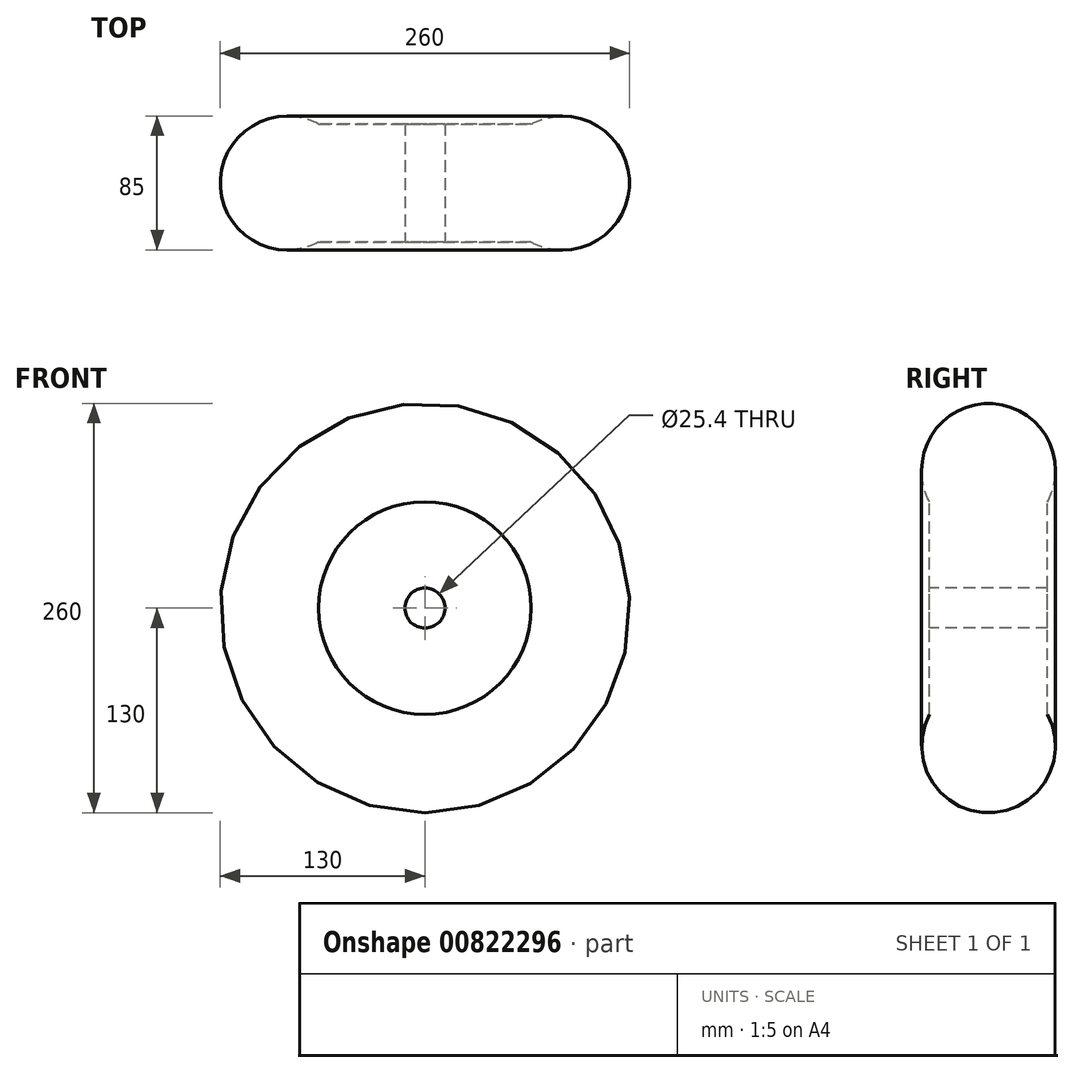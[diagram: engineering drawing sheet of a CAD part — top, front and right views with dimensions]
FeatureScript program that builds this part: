
annotation { "Feature Type Name" : "Feature", "Feature Type Description" : "" }
export const myFeature = defineFeature(function(context is Context, id is Id, definition is map)
    precondition{}
    {
        {
            var Q0;
            Q0=qCreatedBy(makeId("Right.planeOp"),FACE);
            var sketch = newSketch(context, id + "F0", { "sketchPlane" : qUnion([Q0])});
            skLineSegment(sketch, "E0", {"start": v(0, 0) * mm, "end": v(0, 130) * mm});
            skLineSegment(sketch, "E1", {"start": v(0, 0) * mm, "end": v(37.5, 0) * mm});
            skLineSegment(sketch, "E2", {"start": v(0, 130) * mm, "end": v(42.5, 130) * mm});
            skLineSegment(sketch, "E3", {"start": v(37.5, 0) * mm, "end": v(37.5, 12.7) * mm});
            skLineSegment(sketch, "E4", {"start": v(37.5, 12.7) * mm, "end": v(0, 12.7) * mm});
            skLineSegment(sketch, "E5", {"start": v(42.5, 130) * mm, "end": v(42.5, 87.5) * mm});
            skCircle(sketch, "E6", {"center": v(0, 87.5) * mm, "radius": 42.5 * mm});
            skLineSegment(sketch, "E7", {"start": v(37.5, 12.7) * mm, "end": v(37.5, 67.5) * mm});
            skLineSegment(sketch, "E8.MirrorCS", {"start": v(0, 0) * mm, "end": v(-37.5, 0) * mm});
            skLineSegment(sketch, "E9.MirrorCS", {"start": v(-37.5, 12.7) * mm, "end": v(-37.5, 67.5) * mm});
            skLineSegment(sketch, "E10.MirrorCS", {"start": v(-37.5, 0) * mm, "end": v(-37.5, 12.7) * mm});
            skLineSegment(sketch, "E11.MirrorCS", {"start": v(-37.5, 12.7) * mm, "end": v(0, 12.7) * mm});
            skSolve(sketch);
        }
        {
            var Q0;
            {var subQ4=sQuery(id+"F0.wireOp",EDGE,"E9.MirrorCS");Q0=makeQuery(id+"F0.imprint","IMPRINT",FACE,{"disambiguationData":[TD([[makeQuery(id+"F0.imprint","IMPRINT",EDGE,{"derivedFrom":subQ4}),-1.0]])]});}
            var Q1;
            {var subQ3=sQuery(id+"F0.wireOp",EDGE,"E4");Q1=makeQuery(id+"F0.imprint","IMPRINT",FACE,{"disambiguationData":[TD([[makeQuery(id+"F0.imprint","IMPRINT",EDGE,{"derivedFrom":subQ3}),-1.0]])]});}
            var Q2;
            {var subQ0=sQuery(id+"F0.wireOp",EDGE,"E6");var subQ1=sQuery(id+"F0.wireOp",EDGE,"E0");var subQ2=makeQuery(id+"F0.imprint","INTERSECT",VERTEX,{"derivedFrom":[subQ1,subQ0]});Q2=makeQuery(id+"F0.imprint","IMPRINT",FACE,{"disambiguationData":[TD([[makeQuery(id+"F0.imprint","IMPRINT",EDGE,{"disambiguationData":[TD([[subQ2,1.0]])],"derivedFrom":subQ0}),1.0]])]});}
            var Q3;
            {var subQ0=sQuery(id+"F0.wireOp",EDGE,"E6");var subQ1=sQuery(id+"F0.wireOp",EDGE,"E0");var subQ2=makeQuery(id+"F0.imprint","INTERSECT",VERTEX,{"derivedFrom":[subQ1,subQ0]});Q3=makeQuery(id+"F0.imprint","IMPRINT",FACE,{"disambiguationData":[TD([[makeQuery(id+"F0.imprint","IMPRINT",EDGE,{"disambiguationData":[TD([[subQ2,-1.0]])],"derivedFrom":subQ0}),1.0]])]});}
            var Q4;
            Q4=sQuery(id+"F0.wireOp",EDGE,"E1");
            revolve(context, id + "F1", {"surfaceOperationType" : NewSurfaceOperationType.NEW, "entities" : qUnion([Q0, Q1, Q2, Q3]), "axis" : qUnion([Q4]), "revolveType" : RevolveType.FULL});
        }
    });
